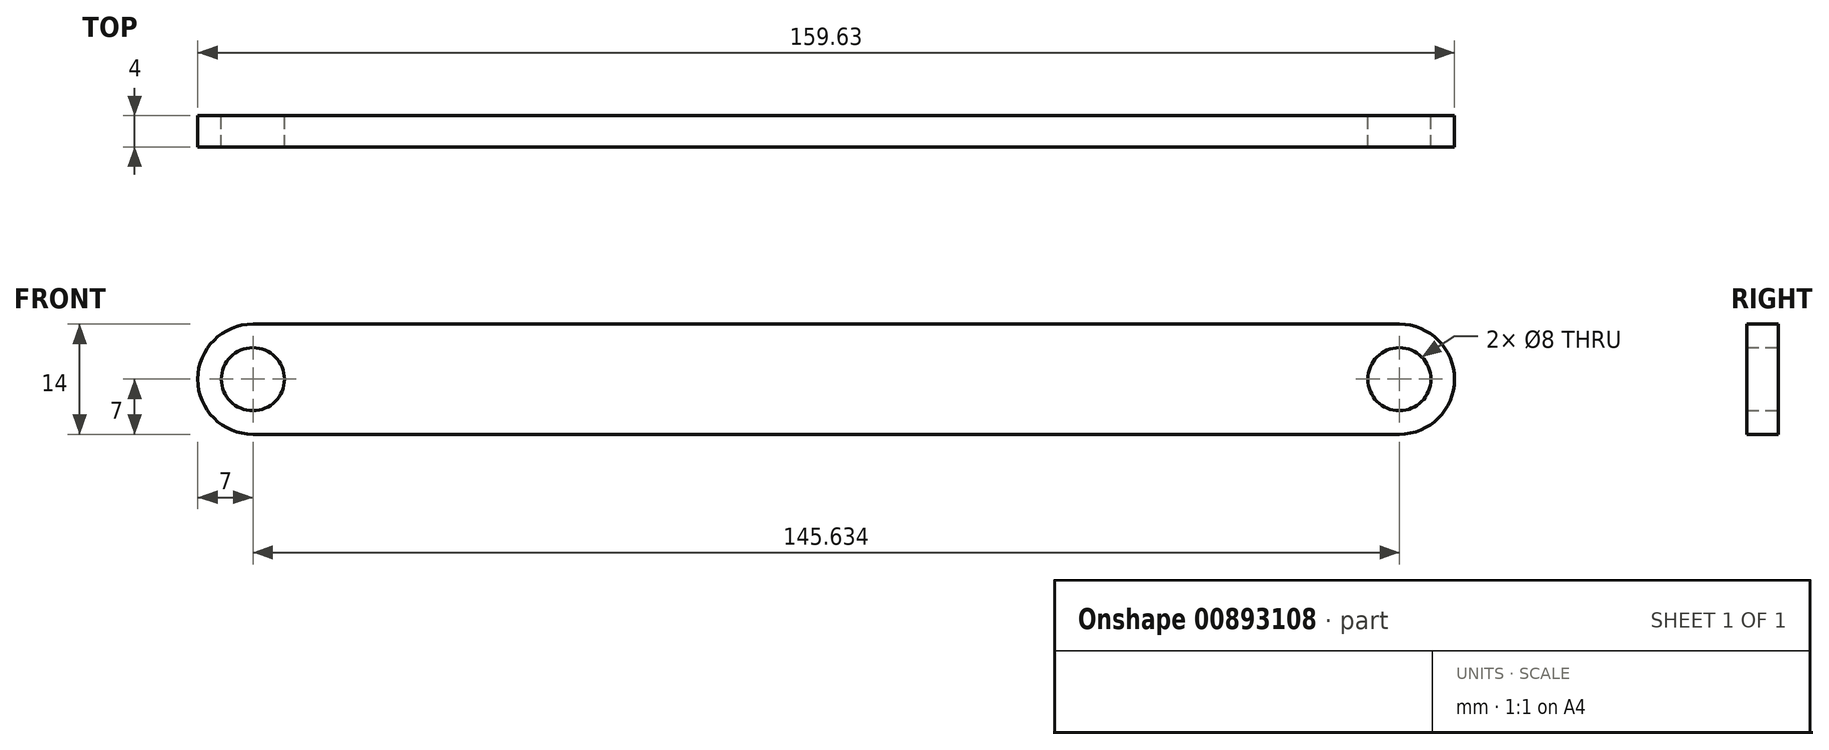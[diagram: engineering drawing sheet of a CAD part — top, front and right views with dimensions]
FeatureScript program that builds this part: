
annotation { "Feature Type Name" : "Feature", "Feature Type Description" : "" }
export const myFeature = defineFeature(function(context is Context, id is Id, definition is map)
    precondition{}
    {
        {
            assignVariable(context, id + "F0", {"name" : "Thickness", "anyValue" : 4});
        }
        {
            var Q0;
            Q0=qCreatedBy(makeId("Front.planeOp"),FACE);
            var sketch = newSketch(context, id + "F1", { "sketchPlane" : qUnion([Q0])});
            skCircle(sketch, "E0", {"center": v(0, 0) * mm, "radius": 4 * mm});
            skCircle(sketch, "E1", {"center": v(145.63, 0) * mm, "radius": 4 * mm});
            skArc(sketch, "E2", {"start": v(145.63, -7) * mm, "mid": v(152.63, 0) * mm, "end": v(145.63, 7) * mm});
            skArc(sketch, "E3", {"start": v(0, 7) * mm, "mid": v(-7, 0) * mm, "end": v(0, -7) * mm});
            skLineSegment(sketch, "E4", {"start": v(0, 7) * mm, "end": v(145.63, 7) * mm});
            skLineSegment(sketch, "E5", {"start": v(0, -7) * mm, "end": v(145.63, -7) * mm});
            skSolve(sketch);
        }
        {
            var Q0;
            Q0=makeQuery(id+"F1.imprint","IMPRINT",FACE,{"disambiguationData":[TD([[makeQuery(id+"F1.imprint","IMPRINT",EDGE,{"derivedFrom":sQuery(id+"F1.wireOp",EDGE,"E0")}),-1.0]])]});
            extrude(context, id + "F2", {"entities" : qUnion([Q0]), "depth" : (getVariable(context, 'Thickness')) * mm, "offsetDistance" : 25 * mm});
        }
    });
